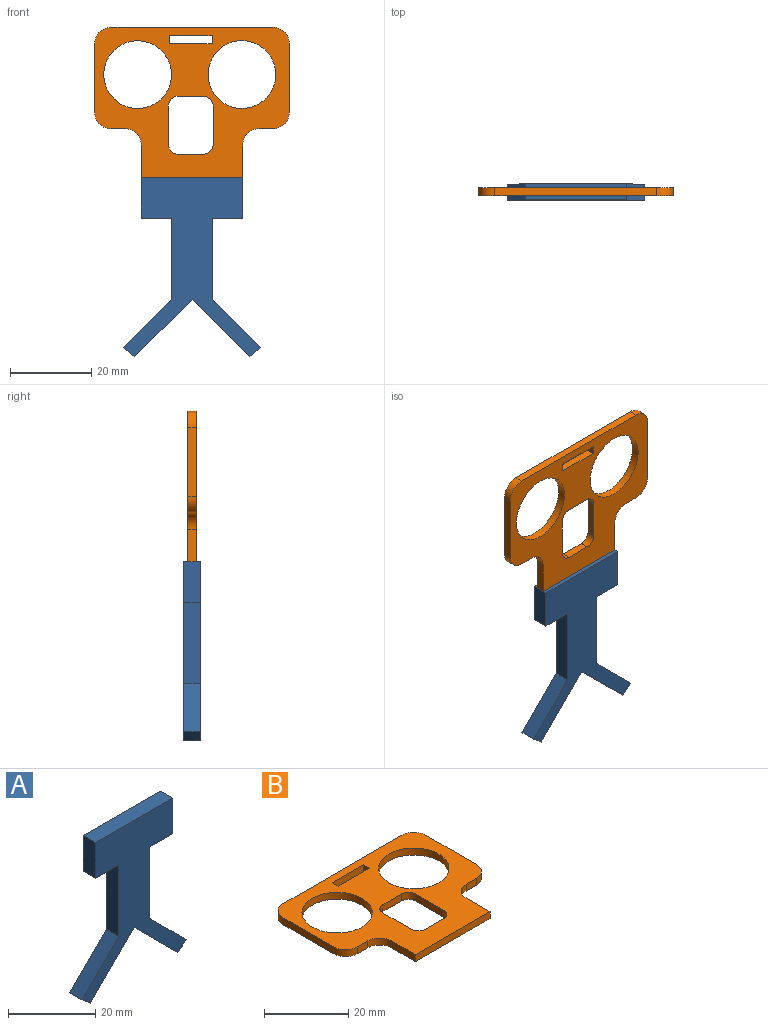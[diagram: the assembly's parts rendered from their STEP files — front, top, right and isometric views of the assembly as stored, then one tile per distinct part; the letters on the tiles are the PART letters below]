
ASSEMBLY  parts=2 mates=1
PART A: 15 faces, bbox 33.8x4x44.1 mm
  f0: plane 7.5x4mm, normal (0,0,-1), area 30mm2, adj f1,f12,f13,f14
  f1: plane 20x4mm, normal (-1,0,0), area 80mm2, adj f0,f2,f13,f14
  f2: plane 11.89x11.89mm, normal (-0.71,0,0.71), area 67.3mm2, adj f1,f3,f13,f14
  f3: plane 4x2.75mm, normal (-0.63,0,-0.77), area 14.2mm2, adj f2,f4,f13,f14
  f4: plane 14.14x14.14mm, normal (0.71,0,-0.71), area 80mm2, adj f3,f5,f13,f14
  f5: plane 14.14x14.14mm, normal (-0.71,0,-0.71), area 80mm2, adj f4,f6,f13,f14
  f6: plane 4x2.75mm, normal (0.63,0,-0.77), area 14.2mm2, adj f5,f7,f13,f14
  f7: plane 11.89x11.89mm, normal (0.71,0,0.71), area 67.3mm2, adj f6,f8,f13,f14
  f8: plane 20x4mm, normal (1,0,0), area 80mm2, adj f7,f9,f13,f14
  f9: plane 7.5x4mm, normal (0,0,-1), area 30mm2, adj f8,f10,f13,f14
  f10: plane 10x4mm, normal (1,0,0), area 40mm2, adj f9,f11,f13,f14
  f11: plane 25x4mm, normal (0,0,1), area 100mm2, adj f10,f12,f13,f14
  f12: plane 10x4mm, normal (-1,0,0), area 40mm2, adj f0,f11,f13,f14
  f13: plane 44.14x33.78mm, normal (0,-1,0), area 580.2mm2, adj f0,f1,f2,f3,f4,f5,f6,f7
  f14: plane 44.14x33.78mm, normal (0,1,0), area 580.2mm2, adj f0,f1,f2,f3,f4,f5,f6,f7
PART B: 30 faces, bbox 47.9x37x2 mm
  f0: plane 47.9x37mm, normal (0,0,1), area 879.6mm2, adj f2,f3,f4,f5,f6,f7,f8,f9
  f1: plane 47.9x37mm, normal (0,0,-1), area 879.6mm2, adj f2,f3,f4,f5,f6,f7,f8,f9
  f2: plane 8x2mm, normal (1,0,0), area 16mm2, adj f0,f1,f10,f20
  f3: plane 3.45x2mm, normal (0,-1,0), area 6.9mm2, adj f0,f1,f20,f23
  f4: plane 17x2mm, normal (1,0,0), area 34mm2, adj f0,f1,f23,f24
  f5: plane 39.9x2mm, normal (0,1,0), area 79.8mm2, adj f0,f1,f24,f25
  f6: plane 17x2mm, normal (-1,0,0), area 34mm2, adj f0,f1,f22,f25
  f7: plane 3.45x2mm, normal (0,-1,0), area 6.9mm2, adj f0,f1,f21,f22
  f8: plane 8x2mm, normal (-1,0,0), area 16mm2, adj f0,f1,f10,f21
  f9: cylinder r=8.35mm len=16.7mm, axis (0,0,-1), area 104.9mm2, adj f0,f1
  f10: plane 25x2mm, normal (0,-1,0), area 50mm2, adj f0,f1,f2,f8
  f11: cylinder r=8.35mm len=16.7mm, axis (0,0,-1), area 104.9mm2, adj f0,f1
  f12: plane 2x2mm, normal (1,0,0), area 4mm2, adj f0,f1,f13,f15
  f13: plane 10.5x2mm, normal (0,1,0), area 21mm2, adj f0,f1,f12,f14
  f14: plane 2x2mm, normal (-1,0,0), area 4mm2, adj f0,f1,f13,f15
  f15: plane 10.5x2mm, normal (0,-1,0), area 21mm2, adj f0,f1,f12,f14
  f16: plane 6.2x2mm, normal (0,-1,0), area 12.4mm2, adj f0,f1,f26,f29
  f17: plane 9.46x2mm, normal (1,0,0), area 18.9mm2, adj f0,f1,f28,f29
  f18: plane 6.2x2mm, normal (0,1,0), area 12.4mm2, adj f0,f1,f27,f28
  f19: plane 9.46x2mm, normal (-1,0,0), area 18.9mm2, adj f0,f1,f26,f27
  f20: cylinder r=4mm len=4mm, axis (0,0,-1), area 12.6mm2, adj f0,f1,f2,f3
  f21: cylinder r=4mm len=4mm, axis (0,0,1), area 12.6mm2, adj f0,f1,f7,f8
  f22: cylinder r=4mm len=4mm, axis (0,0,1), area 12.6mm2, adj f0,f1,f6,f7
  f23: cylinder r=4mm len=4mm, axis (0,0,-1), area 12.6mm2, adj f0,f1,f3,f4
  f24: cylinder r=4mm len=4mm, axis (0,0,1), area 12.6mm2, adj f0,f1,f4,f5
  f25: cylinder r=4mm len=4mm, axis (0,0,-1), area 12.6mm2, adj f0,f1,f5,f6
  f26: cylinder r=2.4mm len=2.4mm, axis (0,0,1), area 7.5mm2, adj f0,f1,f16,f19
  f27: cylinder r=2.4mm len=2.4mm, axis (0,0,-1), area 7.5mm2, adj f0,f1,f18,f19
  f28: cylinder r=2.4mm len=2.4mm, axis (0,0,1), area 7.5mm2, adj f0,f1,f17,f18
  f29: cylinder r=2.4mm len=2.4mm, axis (0,0,-1), area 7.5mm2, adj f0,f1,f16,f17
PLACE A rot(axis=(0,-1,0),0.1deg) t=(0.05,0.06,3.62)mm
PLACE B rot(axis=(1,0,0),90deg) t=(-18.94,-0.94,8.27)mm fixed
MATE parallel A.f11 <-> B.f10  axis (0,0,1) through (-18.93,-1.94,-3.73)mm
